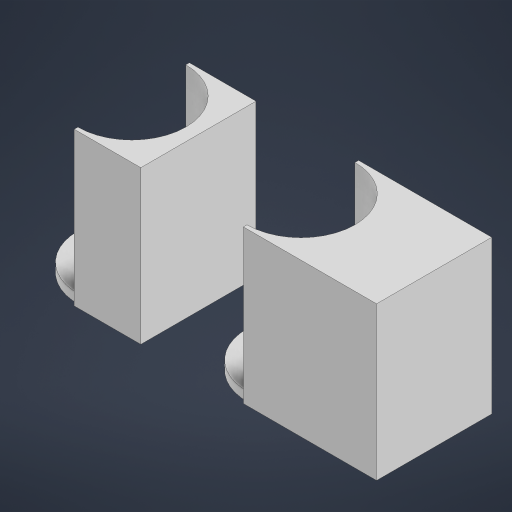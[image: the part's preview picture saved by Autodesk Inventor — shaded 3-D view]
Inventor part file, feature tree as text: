
AUTODESK INVENTOR PART (.ipt)
format: ipt  version: 2023 (Build 270158030, 158C)  size: 178,176 bytes
history: native  units: in
note: dims shown in document units (in); Inventor stores cm internally (conversion verified against a paired STEP export)
features: extrude x2, sketch x1
ambient origin geometry x8: Origin, YZ Plane, XZ Plane, XY Plane, X Axis, Y Axis, Z Axis, Center Point
bodies: Solid3 (feature_tree)
feature tree (3):
  sketch  "Sketch2"  dims[d0=3.8976in d1=1.2598in d2=0.6299in d3=1.9488in d6=1.1811in d7=1.4567in d8=1.1811in d9=1.8504in d10=1.122in d11=0.0in d12=1.6732in d13=0.0in d14=0.0984in d15=0.0in]
  extrude  "Extrusion2"  Depth=1.2598in
  extrude  "Extrusion3"  Depth=0.0984in
